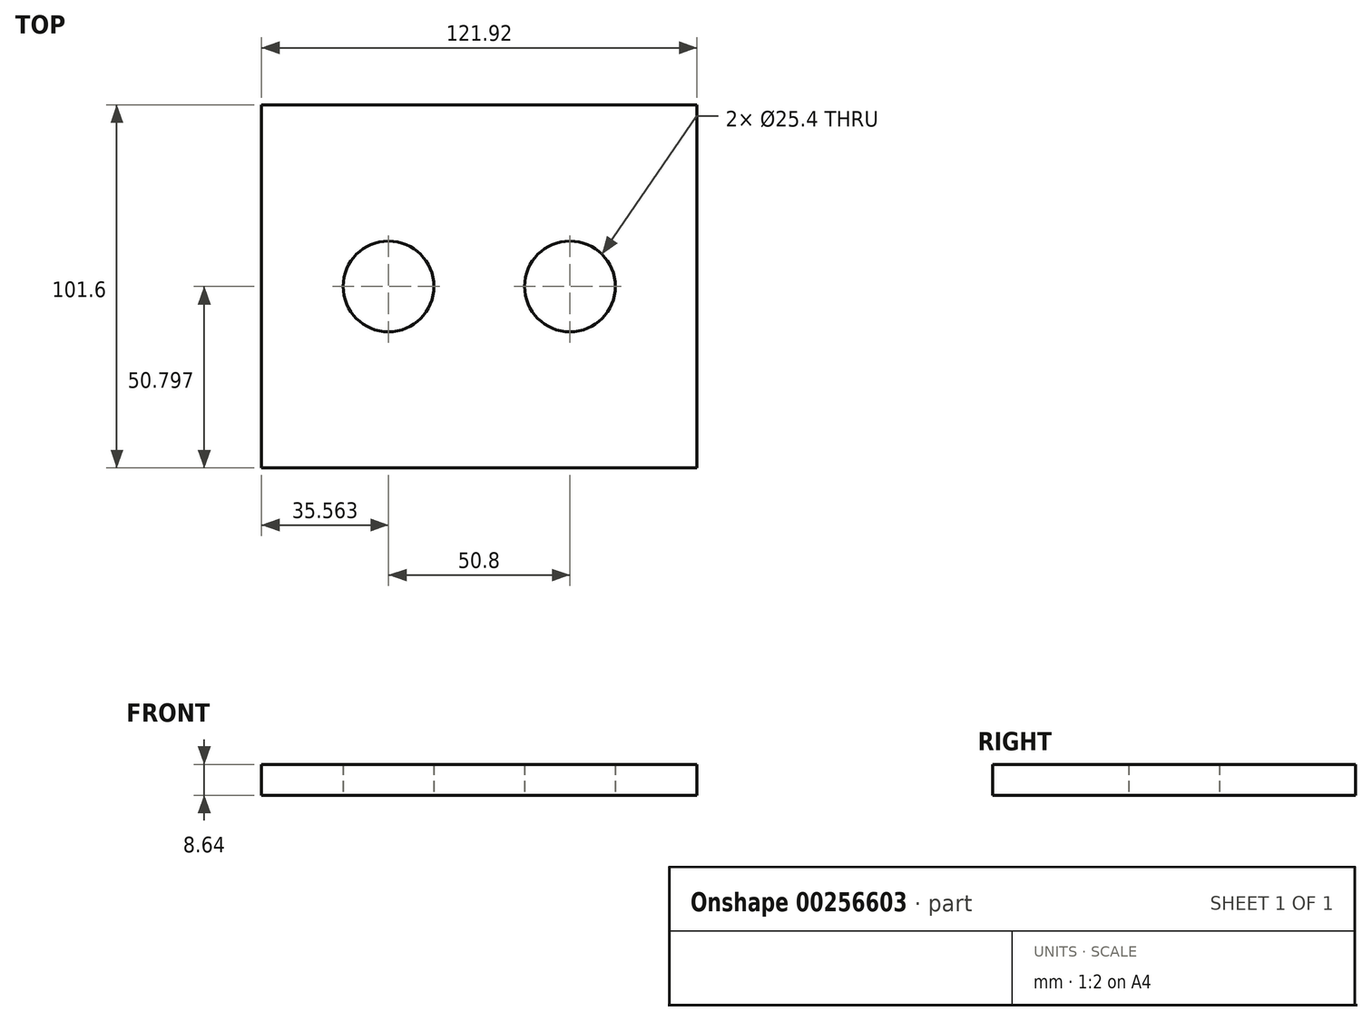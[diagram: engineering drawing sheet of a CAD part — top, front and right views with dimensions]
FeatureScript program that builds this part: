
annotation { "Feature Type Name" : "Feature", "Feature Type Description" : "" }
export const myFeature = defineFeature(function(context is Context, id is Id, definition is map)
    precondition{}
    {
        {
            var Q0;
            Q0=qCreatedBy(makeId("Top.planeOp"),FACE);
            var sketch = newSketch(context, id + "F0", { "sketchPlane" : qUnion([Q0])});
            skLineSegment(sketch, "E0.bottom", {"start": v(-63.12, 69.1) * mm, "end": v(58.8, 69.1) * mm});
            skLineSegment(sketch, "E0.top", {"start": v(-63.12, -32.5) * mm, "end": v(58.8, -32.5) * mm});
            skLineSegment(sketch, "E0.left", {"start": v(-63.12, 69.1) * mm, "end": v(-63.12, -32.5) * mm});
            skLineSegment(sketch, "E0.right", {"start": v(58.8, 69.1) * mm, "end": v(58.8, -32.5) * mm});
            skCircle(sketch, "E1", {"center": v(-27.56, 18.3) * mm, "radius": 12.7 * mm});
            skCircle(sketch, "E2", {"center": v(23.24, 18.3) * mm, "radius": 12.7 * mm});
            skSolve(sketch);
        }
        {
            var Q0;
            Q0=qSketchRegion(id+"F0",true);
            extrude(context, id + "F1", {"entities" : qUnion([Q0]), "depth" : 8.64 * mm});
        }
    });
